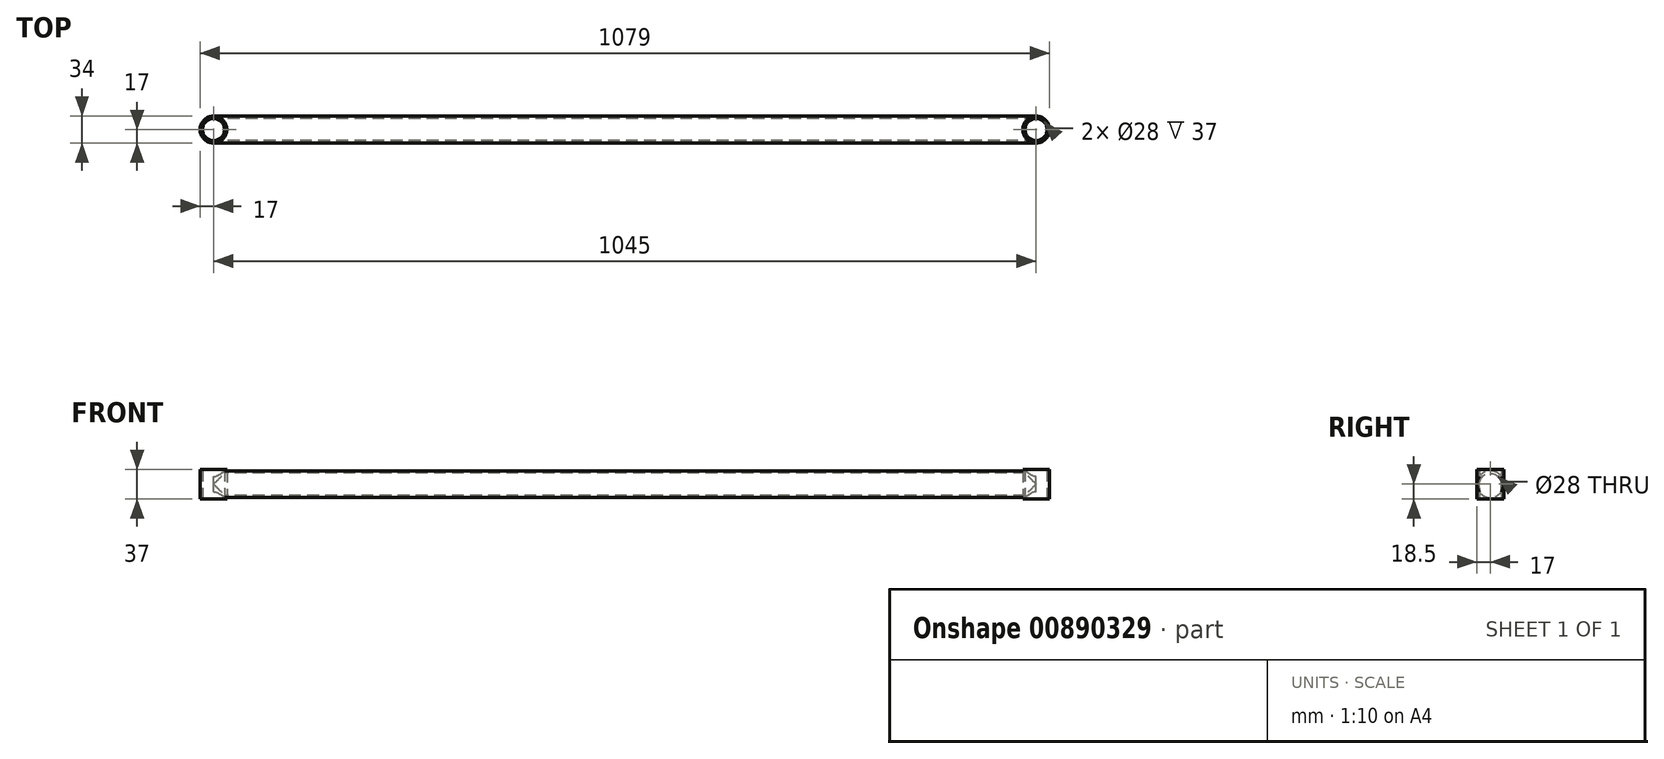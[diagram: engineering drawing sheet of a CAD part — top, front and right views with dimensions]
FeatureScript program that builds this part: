
annotation { "Feature Type Name" : "Feature", "Feature Type Description" : "" }
export const myFeature = defineFeature(function(context is Context, id is Id, definition is map)
    precondition{}
    {
        {
            var Q0;
            Q0=qCreatedBy(makeId("Top.planeOp"),FACE);
            var sketch = newSketch(context, id + "F0", { "sketchPlane" : qUnion([Q0])});
            skLineSegment(sketch, "E0", {"start": v(-500, 0) * mm, "end": v(545, 0) * mm});
            skCircle(sketch, "E1", {"center": v(-500, 0) * mm, "radius": 17 * mm});
            skCircle(sketch, "E2", {"center": v(545, 0) * mm, "radius": 17 * mm});
            skCircle(sketch, "E3", {"center": v(-500, 0) * mm, "radius": 14 * mm});
            skCircle(sketch, "E4", {"center": v(545, 0) * mm, "radius": 14 * mm});
            skSolve(sketch);
        }
        {
            var Q0;
            Q0 = qSketchRegion(id + "F0", true);
            extrude(context, id + "F1", {"entities" : qUnion([Q0]), "depth" : 18.5 * mm, "offsetDistance" : 25 * mm, "hasSecondDirection" : true, "secondDirectionOppositeDirection" : true, "secondDirectionDepth" : 18.5 * mm});
        }
        {
            var Q0;
            Q0=sQuery(id+"F0.wireOp",EDGE,"E0");
            cPlane(context, id + "F2", {"entities" : qUnion([Q0]), "cplaneType" : CPlaneType.MID_PLANE, "offset" : 25 * mm, "width" : 150 * mm, "height" : 150 * mm});
        }
        {
            var Q0;
            Q0=qCreatedBy(id+"F2.planeOp",FACE);
            var sketch = newSketch(context, id + "F3", { "sketchPlane" : qUnion([Q0])});
            skCircle(sketch, "E5", {"center": v(0, 0) * mm, "radius": 17 * mm});
            skCircle(sketch, "E6", {"center": v(0, 0) * mm, "radius": 14 * mm});
            skSolve(sketch);
        }
        {
            var Q0;
            Q0 = qSketchRegion(id + "F3", true);
            extrude(context, id + "F4", {"entities" : qUnion([Q0]), "depth" : 522.5 * mm, "offsetDistance" : 25 * mm, "hasSecondDirection" : true, "secondDirectionOppositeDirection" : true, "secondDirectionDepth" : 522.5 * mm});
        }
        {
            var Q0;
            Q0=makeQuery(id+"F1.opExtrude","CAP_FACE",FACE,{"disambiguationData":[OSD([sQuery(id+"F0.wireOp",EDGE,"E1"),sQuery(id+"F0.wireOp",EDGE,"E3")])],"isStart":false});
            var sketch = newSketch(context, id + "F5", { "sketchPlane" : qUnion([Q0])});
            skCircle(sketch, "E7", {"center": v(-500, 0) * mm, "radius": 14 * mm});
            skSolve(sketch);
        }
        {
            var Q0;
            Q0 = qSketchRegion(id + "F5", true);
            extrude(context, id + "F6", {"entities" : qUnion([Q0]), "operationType" : NewBodyOperationType.REMOVE, "oppositeDirection" : true, "depth" : 50 * mm, "offsetDistance" : 25 * mm});
        }
        {
            var Q0;
            Q0=makeQuery(id+"F1.opExtrude","CAP_FACE",FACE,{"disambiguationData":[OSD([sQuery(id+"F0.wireOp",EDGE,"E2"),sQuery(id+"F0.wireOp",EDGE,"E4")])],"isStart":false});
            var sketch = newSketch(context, id + "F7", { "sketchPlane" : qUnion([Q0])});
            skCircle(sketch, "E8", {"center": v(545, 0) * mm, "radius": 14 * mm});
            skSolve(sketch);
        }
        {
            var Q0;
            Q0 = qSketchRegion(id + "F7", true);
            extrude(context, id + "F8", {"entities" : qUnion([Q0]), "operationType" : NewBodyOperationType.REMOVE, "oppositeDirection" : true, "depth" : 50 * mm, "offsetDistance" : 25 * mm});
        }
    });
